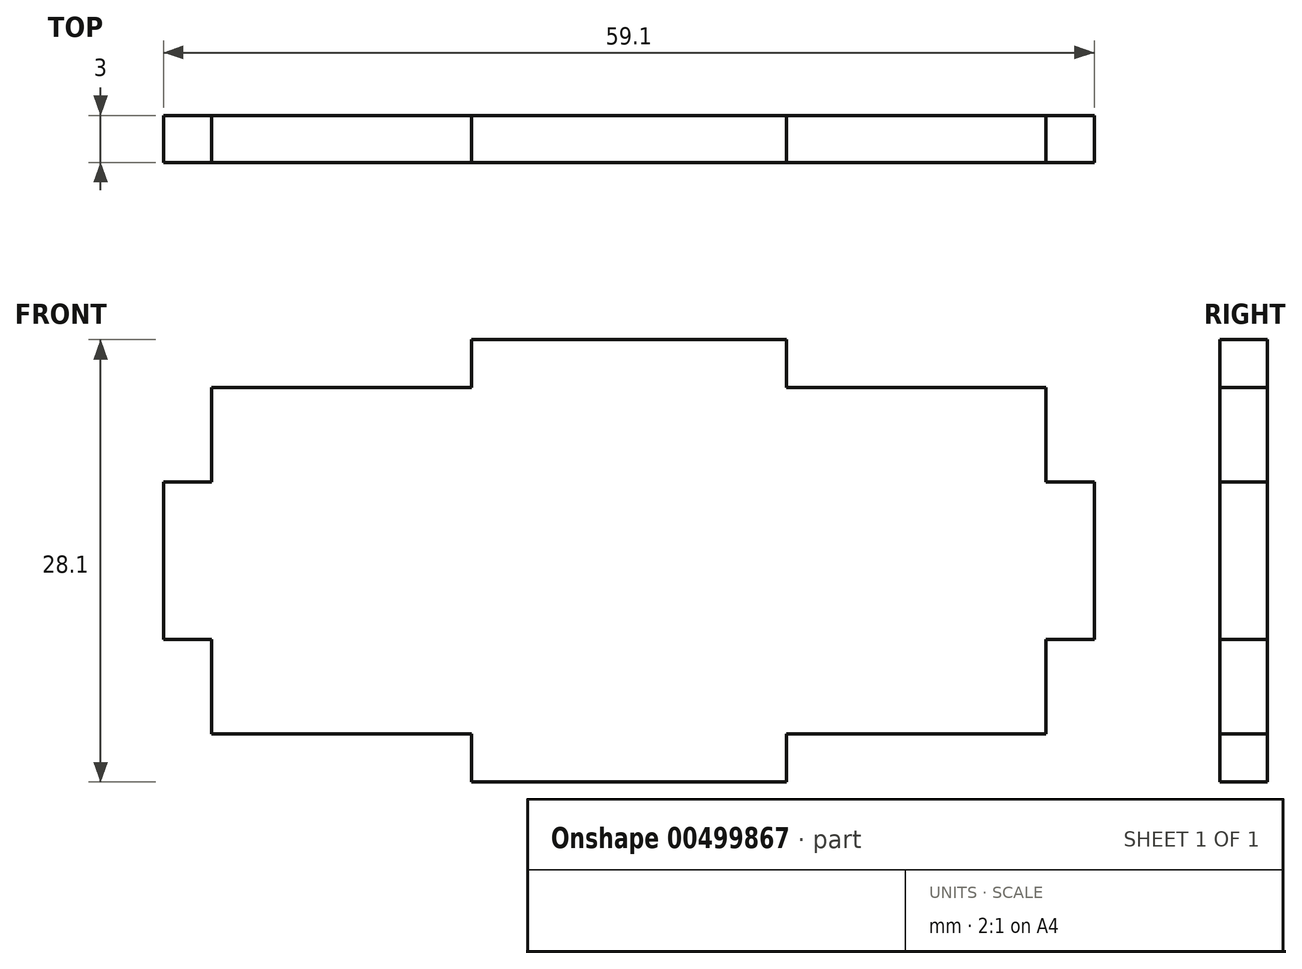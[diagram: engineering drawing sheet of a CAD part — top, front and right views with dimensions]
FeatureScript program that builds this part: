
annotation { "Feature Type Name" : "Feature", "Feature Type Description" : "" }
export const myFeature = defineFeature(function(context is Context, id is Id, definition is map)
    precondition{}
    {
        {
            var Q0;
            Q0=qCreatedBy(makeId("Front.planeOp"),FACE);
            var sketch = newSketch(context, id + "F0", { "sketchPlane" : qUnion([Q0])});
            skLineSegment(sketch, "E0.bottom", {"start": v(26.5, -11) * mm, "end": v(-26.5, -11) * mm});
            skLineSegment(sketch, "E0.top", {"start": v(26.5, 11) * mm, "end": v(-26.5, 11) * mm});
            skLineSegment(sketch, "E0.left", {"start": v(26.5, -11) * mm, "end": v(26.5, 11) * mm});
            skLineSegment(sketch, "E0.right", {"start": v(-26.5, -11) * mm, "end": v(-26.5, 11) * mm});
            skPoint(sketch, "E0.middle", {"position": v(0, 0) * mm});
            skLineSegment(sketch, "E1.bottom", {"start": v(10, -14.05) * mm, "end": v(-10, -14.05) * mm});
            skLineSegment(sketch, "E1.top", {"start": v(10, -11) * mm, "end": v(-10, -11) * mm});
            skLineSegment(sketch, "E1.left", {"start": v(10, -14.05) * mm, "end": v(10, -11) * mm});
            skLineSegment(sketch, "E1.right", {"start": v(-10, -14.05) * mm, "end": v(-10, -11) * mm});
            skPoint(sketch, "E1.middle", {"position": v(0, -12.52) * mm});
            skLineSegment(sketch, "E2.bottom", {"start": v(10, 11) * mm, "end": v(-10, 11) * mm});
            skLineSegment(sketch, "E2.top", {"start": v(10, 14.05) * mm, "end": v(-10, 14.05) * mm});
            skLineSegment(sketch, "E2.left", {"start": v(10, 11) * mm, "end": v(10, 14.05) * mm});
            skLineSegment(sketch, "E2.right", {"start": v(-10, 11) * mm, "end": v(-10, 14.05) * mm});
            skPoint(sketch, "E2.middle", {"position": v(0, 12.52) * mm});
            skLineSegment(sketch, "E3.bottom", {"start": v(-26.5, -5) * mm, "end": v(-29.55, -5) * mm});
            skLineSegment(sketch, "E3.top", {"start": v(-26.5, 5) * mm, "end": v(-29.55, 5) * mm});
            skLineSegment(sketch, "E3.left", {"start": v(-26.5, -5) * mm, "end": v(-26.5, 5) * mm});
            skLineSegment(sketch, "E3.right", {"start": v(-29.55, -5) * mm, "end": v(-29.55, 5) * mm});
            skPoint(sketch, "E3.middle", {"position": v(-28.02, 0) * mm});
            skLineSegment(sketch, "E4.bottom", {"start": v(29.55, -5) * mm, "end": v(26.5, -5) * mm});
            skLineSegment(sketch, "E4.top", {"start": v(29.55, 5) * mm, "end": v(26.5, 5) * mm});
            skLineSegment(sketch, "E4.left", {"start": v(29.55, -5) * mm, "end": v(29.55, 5) * mm});
            skLineSegment(sketch, "E4.right", {"start": v(26.5, -5) * mm, "end": v(26.5, 5) * mm});
            skPoint(sketch, "E4.middle", {"position": v(28.02, 0) * mm});
            skSolve(sketch);
        }
        {
            var Q0;
            Q0 = qSketchRegion(id + "F0", true);
            extrude(context, id + "F1", {"entities" : qUnion([Q0]), "depth" : 3 * mm});
        }
    });
